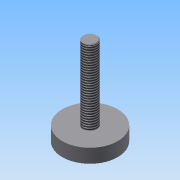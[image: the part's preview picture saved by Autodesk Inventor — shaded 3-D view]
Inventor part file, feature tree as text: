
AUTODESK INVENTOR PART (.ipt)
format: ipt  version: 2015 (Build 190159000, 159)  size: 84,992 bytes
history: native  units: mm
features: extrude x2, sketch x2, thread x1, chamfer x1
ambient origin geometry x8: Origin, YZ Plane, XZ Plane, XY Plane, X Axis, Y Axis, Z Axis, Center Point
bodies: 实体1 (feature_tree)
feature tree (6):
  extrude  "拉伸1"  Depth=5.0mm TaperAngle=0.0deg
  extrude  "拉伸2"  Depth=27.0mm TaperAngle=0.0deg
  thread  "螺纹1"  [1 undecoded]
  chamfer  "倒角1"  Distance=0.25mm Angle=45.0deg
  sketch  "草图1"  dims[d0=20.0mm d1=5.0mm d2=0.0mm]
  sketch  "草图2"  dims[d3=5.0mm d4=27.0mm d5=0.0mm d6=10.0mm d7=0.0mm d8=0.25mm d9=2.0mm d10=45.0deg]
note: 1 required parameter value undecoded (feature->parameter linkage not recoverable at this tier; creation-order binding heuristic only, values carry confidence <= 0.55)
